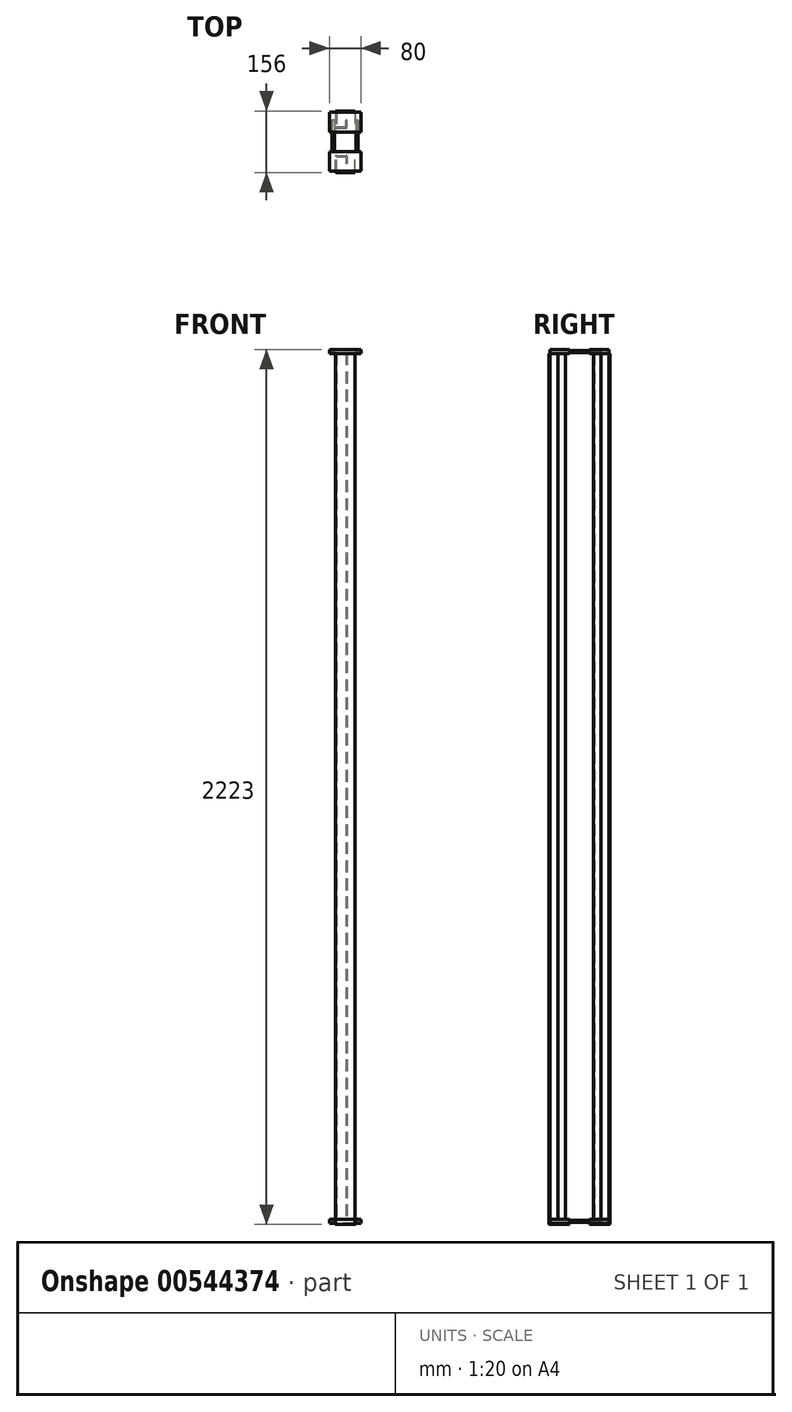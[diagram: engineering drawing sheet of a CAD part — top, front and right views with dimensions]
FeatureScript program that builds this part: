
annotation { "Feature Type Name" : "Feature", "Feature Type Description" : "" }
export const myFeature = defineFeature(function(context is Context, id is Id, definition is map)
    precondition{}
    {
        {
            var Q0;
            Q0=qCreatedBy(makeId("Front.planeOp"),FACE);
            cPlane(context, id + "F0", {"entities" : qUnion([Q0]), "cplaneType" : CPlaneType.OFFSET, "offset" : 25 * mm, "width" : 150 * mm, "height" : 150 * mm});
        }
        {
            var Q0;
            Q0=qCreatedBy(id+"F0.planeOp",FACE);
            var sketch = newSketch(context, id + "F1", { "sketchPlane" : qUnion([Q0])});
            skLineSegment(sketch, "E0.bottom", {"start": v(-40, 1110) * mm, "end": v(40, 1110) * mm});
            skLineSegment(sketch, "E0.top", {"start": v(-40, 1100) * mm, "end": v(40, 1100) * mm});
            skLineSegment(sketch, "E0.left", {"start": v(-40, 1110) * mm, "end": v(-40, 1100) * mm});
            skLineSegment(sketch, "E0.right", {"start": v(40, 1110) * mm, "end": v(40, 1100) * mm});
            skLineSegment(sketch, "E1.bottom", {"start": v(-40, -1100) * mm, "end": v(40, -1100) * mm});
            skLineSegment(sketch, "E1.top", {"start": v(-40, -1110) * mm, "end": v(40, -1110) * mm});
            skLineSegment(sketch, "E1.left", {"start": v(-40, -1100) * mm, "end": v(-40, -1110) * mm});
            skLineSegment(sketch, "E1.right", {"start": v(40, -1100) * mm, "end": v(40, -1110) * mm});
            skSolve(sketch);
        }
        {
            var Q0;
            Q0 = qSketchRegion(id + "F1", true);
            extrude(context, id + "F2", {"entities" : qUnion([Q0]), "depth" : 50 * mm, "offsetDistance" : 25 * mm});
        }
        {
            var Q0;
            Q0=qCreatedBy(makeId("Right.planeOp"),FACE);
            var sketch = newSketch(context, id + "F3", { "sketchPlane" : qUnion([Q0])});
            skLineSegment(sketch, "E2.0", {"start": v(-75, 1110) * mm, "end": v(-25, 1110) * mm});
            skLineSegment(sketch, "E3.0", {"start": v(-75, -1110) * mm, "end": v(-25, -1110) * mm});
            skLineSegment(sketch, "E4", {"start": v(-75, 1110) * mm, "end": v(-75, -1110) * mm});
            skLineSegment(sketch, "E5.0", {"start": v(-75, 1113) * mm, "end": v(-25, 1113) * mm});
            skLineSegment(sketch, "E5.1", {"start": v(-78, 1110) * mm, "end": v(-78, -1110) * mm});
            skLineSegment(sketch, "E5.2", {"start": v(-75, -1113) * mm, "end": v(-25, -1113) * mm});
            skLineSegment(sketch, "E6", {"start": v(-25, -1110) * mm, "end": v(-25, -1113) * mm});
            skLineSegment(sketch, "E7", {"start": v(-25, 1110) * mm, "end": v(-25, 1113) * mm});
            skPoint(sketch, "E8.visualSharp", {"position": v(-78, -1113) * mm});
            skArc(sketch, "E8.filletArc", {"start": v(-78, -1110) * mm, "mid": v(-77.12, -1112.12) * mm, "end": v(-75, -1113) * mm});
            skPoint(sketch, "E9.visualSharp", {"position": v(-78, 1113) * mm});
            skArc(sketch, "E9.filletArc", {"start": v(-75, 1113) * mm, "mid": v(-77.12, 1112.12) * mm, "end": v(-78, 1110) * mm});
            skSolve(sketch);
        }
        {
            var Q0;
            Q0=makeQuery(id+"F2.opExtrude","CAP_FACE",FACE,{"disambiguationData":[OSD([sQuery(id+"F1.wireOp",EDGE,"E0.bottom"),sQuery(id+"F1.wireOp",EDGE,"E0.top"),sQuery(id+"F1.wireOp",EDGE,"E0.left"),sQuery(id+"F1.wireOp",EDGE,"E0.right")])],"isStart":true});
            var sketch = newSketch(context, id + "F4", { "sketchPlane" : qUnion([Q0])});
            skLineSegment(sketch, "E10", {"start": v(-40, 1105) * mm, "end": v(40, 1105) * mm, "construction": true});
            skCircle(sketch, "E11", {"center": v(-30, 1105) * mm, "radius": 3 * mm});
            skCircle(sketch, "E12", {"center": v(30, 1105) * mm, "radius": 3 * mm});
            skCircle(sketch, "E13.MirrorC", {"center": v(-30, -1105) * mm, "radius": 3 * mm});
            skCircle(sketch, "E14.MirrorC", {"center": v(30, -1105) * mm, "radius": 3 * mm});
            skSolve(sketch);
        }
        {
            var Q0;
            Q0 = qSketchRegion(id + "F4", true);
            extrude(context, id + "F5", {"entities" : qUnion([Q0]), "depth" : 80 * mm, "offsetDistance" : 25 * mm});
        }
        {
            var Q0;
            Q0=qCreatedBy(makeId("Top.planeOp"),FACE);
            var sketch = newSketch(context, id + "F6", { "sketchPlane" : qUnion([Q0])});
            skLineSegment(sketch, "E15.0", {"start": v(-25, -75) * mm, "end": v(-25, -38) * mm});
            skLineSegment(sketch, "E16.0", {"start": v(-22, -75) * mm, "end": v(-22, -38) * mm});
            skLineSegment(sketch, "E17", {"start": v(-22, -35) * mm, "end": v(2, -35) * mm});
            skLineSegment(sketch, "E18", {"start": v(5, -38) * mm, "end": v(5, -55) * mm});
            skLineSegment(sketch, "E19.0", {"start": v(2, -38) * mm, "end": v(2, -55) * mm});
            skLineSegment(sketch, "E19.1", {"start": v(-22, -38) * mm, "end": v(2, -38) * mm});
            skLineSegment(sketch, "E20", {"start": v(5, -55) * mm, "end": v(2, -55) * mm});
            skPoint(sketch, "E21.orphan", {"position": v(-25, -25) * mm});
            skPoint(sketch, "E22.visualSharp", {"position": v(-25, -35) * mm});
            skArc(sketch, "E22.filletArc", {"start": v(-22, -35) * mm, "mid": v(-24.12, -35.88) * mm, "end": v(-25, -38) * mm});
            skPoint(sketch, "E23.visualSharp", {"position": v(5, -35) * mm});
            skArc(sketch, "E23.filletArc", {"start": v(5, -38) * mm, "mid": v(4.12, -35.88) * mm, "end": v(2, -35) * mm});
            skLineSegment(sketch, "E24", {"start": v(-22, -78) * mm, "end": v(25, -78) * mm});
            skPoint(sketch, "E25.orphan", {"position": v(-25, -75) * mm});
            skLineSegment(sketch, "E26", {"start": v(-22, -75) * mm, "end": v(25, -75) * mm});
            skLineSegment(sketch, "E27", {"start": v(25, -75) * mm, "end": v(25, -78) * mm});
            skPoint(sketch, "E28.visualSharp", {"position": v(-25, -78) * mm});
            skArc(sketch, "E28.filletArc", {"start": v(-25, -75) * mm, "mid": v(-24.12, -77.12) * mm, "end": v(-22, -78) * mm});
            skSolve(sketch);
        }
        {
            var Q0;
            Q0 = qSketchRegion(id + "F6", true);
            extrude(context, id + "F7", {"entities" : qUnion([Q0]), "endBound" : BoundingType.SYMMETRIC, "depth" : 2200 * mm, "offsetDistance" : 25 * mm});
        }
        {
            var Q0;
            Q0=qCreatedBy(makeId("Right.planeOp"),FACE);
            var sketch = newSketch(context, id + "F8", { "sketchPlane" : qUnion([Q0])});
            skLineSegment(sketch, "E29.0", {"start": v(-75, -1100) * mm, "end": v(-75, -1110) * mm});
            skLineSegment(sketch, "E29.1", {"start": v(-75, -1110) * mm, "end": v(-25, -1110) * mm});
            skLineSegment(sketch, "E30.0", {"start": v(-75, -1113) * mm, "end": v(-25, -1113) * mm});
            skLineSegment(sketch, "E30.1", {"start": v(-78, -1100) * mm, "end": v(-78, -1110) * mm});
            skLineSegment(sketch, "E31", {"start": v(-25, -1110) * mm, "end": v(-25, -1113) * mm});
            skPoint(sketch, "E32.visualSharp", {"position": v(-78, -1113) * mm});
            skArc(sketch, "E32.filletArc", {"start": v(-78, -1110) * mm, "mid": v(-77.12, -1112.12) * mm, "end": v(-75, -1113) * mm});
            skArc(sketch, "E33.MirrorCS", {"start": v(-78, 1110) * mm, "mid": v(-77.12, 1112.12) * mm, "end": v(-75, 1113) * mm});
            skLineSegment(sketch, "E34.MirrorCS", {"start": v(-25, 1110) * mm, "end": v(-25, 1113) * mm});
            skLineSegment(sketch, "E35.MirrorCS", {"start": v(-75, 1100) * mm, "end": v(-75, 1110) * mm});
            skLineSegment(sketch, "E36.MirrorCS", {"start": v(-78, 1100) * mm, "end": v(-78, 1110) * mm});
            skLineSegment(sketch, "E37.MirrorCS", {"start": v(-75, 1113) * mm, "end": v(-25, 1113) * mm});
            skLineSegment(sketch, "E38.MirrorCS", {"start": v(-75, 1110) * mm, "end": v(-25, 1110) * mm});
            skPoint(sketch, "E39.MirrorP", {"position": v(-78, 1113) * mm});
            skLineSegment(sketch, "E40", {"start": v(-78, -1100) * mm, "end": v(-75, -1100) * mm});
            skLineSegment(sketch, "E41", {"start": v(-78, 1100) * mm, "end": v(-75, 1100) * mm});
            skSolve(sketch);
        }
        {
            var Q0;
            Q0=makeQuery(id+"F8.imprint","IMPRINT",FACE,{"disambiguationData":[TD([[makeQuery(id+"F8.imprint","IMPRINT",EDGE,{"derivedFrom":sQuery(id+"F8.wireOp",EDGE,"E29.0")}),-1.0]])]});
            var Q1;
            Q1=makeQuery(id+"F8.imprint","IMPRINT",FACE,{"disambiguationData":[TD([[makeQuery(id+"F8.imprint","IMPRINT",EDGE,{"derivedFrom":sQuery(id+"F8.wireOp",EDGE,"E33.MirrorCS")}),-1.0]])]});
            extrude(context, id + "F9", {"entities" : qUnion([Q0, Q1]), "endBound" : BoundingType.SYMMETRIC, "depth" : 50 * mm, "offsetDistance" : 25 * mm});
        }
        {
            var Q0;
            Q0=makeQuery(id+"F2.opExtrude","SWEPT_BODY",BODY,{"disambiguationData":[OSD([sQuery(id+"F1.wireOp",EDGE,"E0.bottom"),sQuery(id+"F1.wireOp",EDGE,"E0.top"),sQuery(id+"F1.wireOp",EDGE,"E0.left"),sQuery(id+"F1.wireOp",EDGE,"E0.right")])]});
            var Q1;
            Q1=makeQuery(id+"F2.opExtrude","SWEPT_BODY",BODY,{"disambiguationData":[OSD([sQuery(id+"F1.wireOp",EDGE,"E1.bottom"),sQuery(id+"F1.wireOp",EDGE,"E1.top"),sQuery(id+"F1.wireOp",EDGE,"E1.left"),sQuery(id+"F1.wireOp",EDGE,"E1.right")])]});
            var Q2;
            Q2=makeQuery(id+"FXLR2hJO1yESMgW_2.opExtrude","SWEPT_BODY",BODY,{"disambiguationData":[OSD([sQuery(id+"F3.wireOp",EDGE,"E2.0"),sQuery(id+"F3.wireOp",EDGE,"E3.0"),sQuery(id+"F3.wireOp",EDGE,"E4"),sQuery(id+"F3.wireOp",EDGE,"E5.0"),sQuery(id+"F3.wireOp",EDGE,"E5.1"),sQuery(id+"F3.wireOp",EDGE,"E5.2"),sQuery(id+"F3.wireOp",EDGE,"E6"),sQuery(id+"F3.wireOp",EDGE,"E7"),sQuery(id+"F3.wireOp",EDGE,"E8.filletArc"),sQuery(id+"F3.wireOp",EDGE,"E9.filletArc")])]});
            var Q3;
            Q3=makeQuery(id+"F7.opExtrude","SWEPT_BODY",BODY,{"disambiguationData":[OSD([sQuery(id+"F6.wireOp",EDGE,"E15.0"),sQuery(id+"F6.wireOp",EDGE,"E16.0"),sQuery(id+"F6.wireOp",EDGE,"E17"),sQuery(id+"F6.wireOp",EDGE,"E18"),sQuery(id+"F6.wireOp",EDGE,"E19.0"),sQuery(id+"F6.wireOp",EDGE,"E19.1"),sQuery(id+"F6.wireOp",EDGE,"E20"),sQuery(id+"F6.wireOp",EDGE,"E22.filletArc"),sQuery(id+"F6.wireOp",EDGE,"E23.filletArc"),sQuery(id+"F6.wireOp",EDGE,"E24"),sQuery(id+"F6.wireOp",EDGE,"E26"),sQuery(id+"F6.wireOp",EDGE,"E27"),sQuery(id+"F6.wireOp",EDGE,"E28.filletArc")])]});
            var Q4;
            Q4=makeQuery(id+"F9.opExtrude","SWEPT_BODY",BODY,{"disambiguationData":[OSD([sQuery(id+"F8.wireOp",EDGE,"E33.MirrorCS"),sQuery(id+"F8.wireOp",EDGE,"E34.MirrorCS"),sQuery(id+"F8.wireOp",EDGE,"E35.MirrorCS"),sQuery(id+"F8.wireOp",EDGE,"E36.MirrorCS"),sQuery(id+"F8.wireOp",EDGE,"E37.MirrorCS"),sQuery(id+"F8.wireOp",EDGE,"E38.MirrorCS"),sQuery(id+"F8.wireOp",EDGE,"E41")])]});
            var Q5;
            Q5=makeQuery(id+"F9.opExtrude","SWEPT_BODY",BODY,{"disambiguationData":[OSD([sQuery(id+"F8.wireOp",EDGE,"E29.0"),sQuery(id+"F8.wireOp",EDGE,"E29.1"),sQuery(id+"F8.wireOp",EDGE,"E30.0"),sQuery(id+"F8.wireOp",EDGE,"E30.1"),sQuery(id+"F8.wireOp",EDGE,"E31"),sQuery(id+"F8.wireOp",EDGE,"E32.filletArc"),sQuery(id+"F8.wireOp",EDGE,"E40")])]});
            var Q6;
            Q6=qCreatedBy(makeId("Front.planeOp"),FACE);
            mirror(context, id + "F10", {"entities" : qUnion([Q0, Q1, Q2, Q3, Q4, Q5]), "mirrorPlane" : qUnion([Q6])});
        }
        {
            var Q0;
            Q0=makeQuery(id+"F10.opPattern","COPY",EDGE,{"derivedFrom":makeQuery(id+"F9.opExtrude","CAP_EDGE",EDGE,{"disambiguationData":[OSD([sQuery(id+"F8.wireOp",EDGE,"E36.MirrorCS")])],"isStart":true}),"instanceName":"1"});
            var Q1;
            Q1=makeQuery(id+"F10.opPattern","COPY",EDGE,{"derivedFrom":makeQuery(id+"F9.opExtrude","CAP_EDGE",EDGE,{"disambiguationData":[OSD([sQuery(id+"F8.wireOp",EDGE,"E36.MirrorCS")])],"isStart":false}),"instanceName":"1"});
            var Q2;
            Q2=makeQuery(id+"F9.opExtrude","CAP_EDGE",EDGE,{"disambiguationData":[OSD([sQuery(id+"F8.wireOp",EDGE,"E37.MirrorCS")])],"isStart":false});
            var Q3;
            Q3=makeQuery(id+"F9.opExtrude","CAP_EDGE",EDGE,{"disambiguationData":[OSD([sQuery(id+"F8.wireOp",EDGE,"E37.MirrorCS")])],"isStart":true});
            var Q4;
            Q4=makeQuery(id+"F9.opExtrude","CAP_EDGE",EDGE,{"disambiguationData":[OSD([sQuery(id+"F8.wireOp",EDGE,"E30.1")])],"isStart":true});
            var Q5;
            Q5=makeQuery(id+"F10.opPattern","COPY",EDGE,{"derivedFrom":makeQuery(id+"F9.opExtrude","CAP_EDGE",EDGE,{"disambiguationData":[OSD([sQuery(id+"F8.wireOp",EDGE,"E30.0")])],"isStart":true}),"instanceName":"1"});
            fillet(context, id + "F11", {"entities" : qUnion([Q0, Q1, Q2, Q3, Q4, Q5]), "radius" : 3 * mm, "tangentPropagation" : true, "allowEdgeOverflow" : false});
        }
    });
